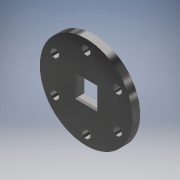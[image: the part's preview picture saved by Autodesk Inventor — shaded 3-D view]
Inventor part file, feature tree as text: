
AUTODESK INVENTOR PART (.ipt)
format: ipt  version: 2019 (Build 230136000, 136)  size: 141,824 bytes
history: native  units: in
note: dims shown in document units (in); Inventor stores cm internally (conversion verified against a paired STEP export)
features: extrude x3, sketch x3, chamfer x1
ambient origin geometry x8: Origin, YZ Plane, XZ Plane, XY Plane, X Axis, Y Axis, Z Axis, Center Point
bodies: Solid1 (feature_tree)
feature tree (7):
  extrude  "Extrusion1"  Depth=0.3125in TaperAngle=0.0deg
  extrude  "Extrusion2"  Depth=2.3622in TaperAngle=360.0deg
  extrude  "Extrusion3"  Depth=0.785in
  chamfer  "Chamfer1"  Distance=0.375in
  sketch  "Sketch1"  dims[d0=3.78in d1=0.3125in d2=0.0in]
  sketch  "Sketch2"  dims[d3=0.348in d5=2.3622in d7=360.0deg]
  sketch  "Sketch3"  dims[d9=0.375in d10=0.0in d11=0.785in d12=0.375in d13=0.0in d14=0.0625in d15=0.125in d16=45.0deg d17=2.9528in]
